# Revit family: Термостатическая головка HERZ-Design-MINI D, с креплением хомутом или клипсой, 9200 99
name_source: partatom
category: Rohrzubehör
units: mm (PartAtom-declared; Revit-internal decimal feet)

## family parameters
Arbeitsebenenbasiert = Nein
Beim Laden mit Abzugskörper schneiden = Nein
Bemaßung runder Anschluss = Durchmesser verwenden
Gemeinsam genutzt = Nein
Immer vertikal = Nein
OmniClass-Nummer = 23.65.55.14
OmniClass-Titel = Valves for Liquid Services
Teiletyp = Normal

## types (1)
- Термостатическая головка HERZ-Design-MINI D, с креплением хомутом или клипсой, 9200 99
    Hersteller = HERZ Armaturen Ges.m.b.H.
    LO1 = 5.5 mm  [stored 0.0180446 ft]
    LO2 = 18.6 mm  [stored 0.0610236 ft]
    S01 = 91.7 mm  [stored 0.300853 ft]
    S02 = 60 mm  [stored 0.19685 ft]
    URL = www.herz-armaturen.at
    Автоматическая защита от замерзания = при прибл. 6 °C
    Диапазон регулирования = 6-28°C
    Исполнение = Термостатическая головка HERZ-Design MINI "D" с жидкостным датчиком (гидросенсором). Предназначается только для радиаторов со встроенным клапаном (например, Vogel & Noot). Цвет маховика - белый.
    Маховик = Пластик, белый
    Номер заказа = 1920099
    Область применения = Для монтажа на всех HERZ-клапанах, предназначенных для термостатической работы.
    Принцип действия = HERZ-термостатическая головка является датчиком прямого регулирования.
Изменение объема жидкости в HERZ-гидросенсоре приводит в движение шток клапана.

note: [stored X ft] marks values corroborated as IEEE doubles in the binary element streams (Revit-internal decimal feet)
